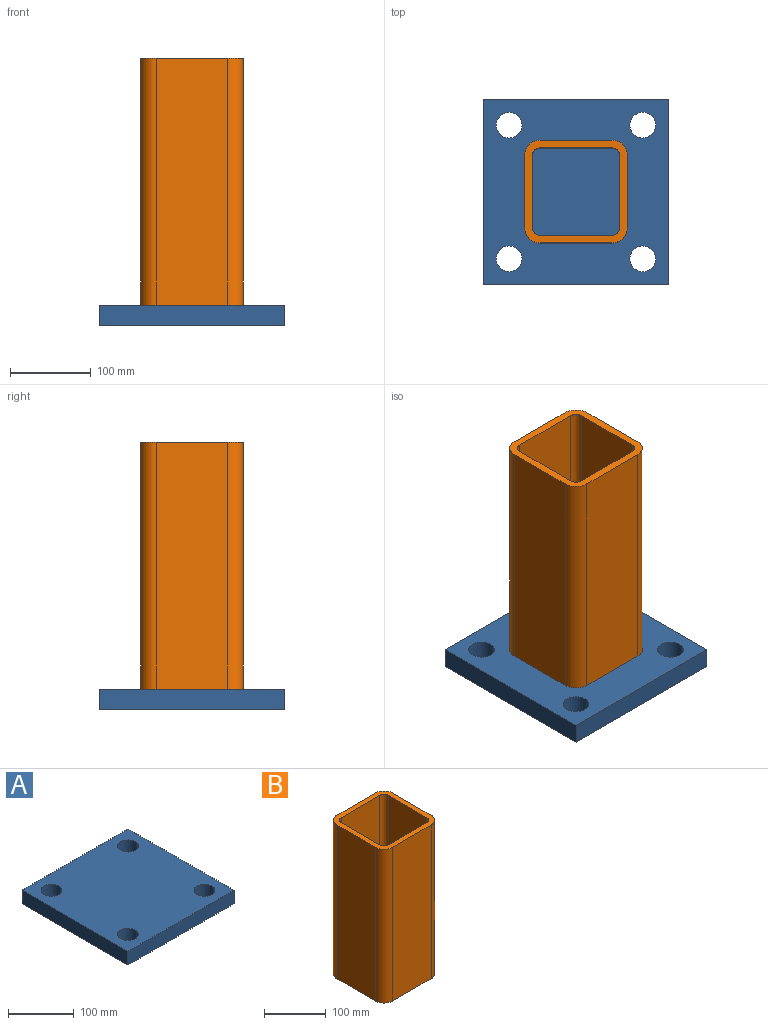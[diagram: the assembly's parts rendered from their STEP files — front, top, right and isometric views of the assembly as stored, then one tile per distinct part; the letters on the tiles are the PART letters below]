
ASSEMBLY  parts=2 mates=1
PART A: 10 faces, bbox 228.6x228.6x25.4 mm
  f0: plane 228.6x25.4mm, normal (-1,0,0), area 5806.4mm2, adj f1,f6,f8,f9
  f1: plane 228.6x25.4mm, normal (0,-1,0), area 5806.4mm2, adj f0,f2,f8,f9
  f2: plane 228.6x25.4mm, normal (1,0,0), area 5806.4mm2, adj f1,f6,f8,f9
  f3: cylinder r=15.88mm len=31.75mm, axis (0,0,-1), area 2533.5mm2, adj f8,f9
  f4: cylinder r=15.88mm len=31.75mm, axis (0,0,-1), area 2533.5mm2, adj f8,f9
  f5: cylinder r=15.88mm len=31.75mm, axis (0,0,-1), area 2533.5mm2, adj f8,f9
  f6: plane 228.6x25.4mm, normal (0,1,0), area 5806.4mm2, adj f0,f2,f8,f9
  f7: cylinder r=15.88mm len=31.75mm, axis (0,0,-1), area 2533.5mm2, adj f8,f9
  f8: plane 228.6x228.6mm, normal (0,0,1), area 49091mm2, adj f0,f1,f2,f3,f4,f5,f6,f7
  f9: plane 228.6x228.6mm, normal (0,0,-1), area 49091mm2, adj f0,f1,f2,f3,f4,f5,f6,f7
PART B: 18 faces, bbox 127x127x304.8 mm
  f0: plane 304.8x88.9mm, normal (0,-1,0), area 27096.7mm2, adj f1,f15,f16,f17
  f1: cylinder r=19.05mm len=304.8mm, axis (0,0,-1), area 9120.7mm2, adj f0,f2,f16,f17
  f2: plane 304.8x88.9mm, normal (1,0,0), area 27096.7mm2, adj f1,f3,f16,f17
  f3: cylinder r=19.05mm len=304.8mm, axis (0,0,-1), area 9120.7mm2, adj f2,f4,f16,f17
  f4: plane 304.8x88.9mm, normal (0,1,0), area 27096.7mm2, adj f3,f5,f16,f17
  f5: cylinder r=19.05mm len=304.8mm, axis (0,0,-1), area 9120.7mm2, adj f4,f6,f16,f17
  f6: plane 304.8x88.9mm, normal (-1,0,0), area 27096.7mm2, adj f5,f15,f16,f17
  f7: cylinder r=9.53mm len=304.8mm, axis (0,0,-1), area 4560.4mm2, adj f8,f14,f16,f17
  f8: plane 304.8x88.9mm, normal (1,0,0), area 27096.7mm2, adj f7,f9,f16,f17
  f9: cylinder r=9.53mm len=304.8mm, axis (0,0,-1), area 4560.4mm2, adj f8,f10,f16,f17
  f10: plane 304.8x88.9mm, normal (0,-1,0), area 27096.7mm2, adj f9,f11,f16,f17
  f11: cylinder r=9.53mm len=304.8mm, axis (0,0,-1), area 4560.4mm2, adj f10,f12,f16,f17
  f12: plane 304.8x88.9mm, normal (-1,0,0), area 27096.7mm2, adj f11,f13,f16,f17
  f13: cylinder r=9.53mm len=304.8mm, axis (0,0,-1), area 4560.4mm2, adj f12,f14,f16,f17
  f14: plane 304.8x88.9mm, normal (0,1,0), area 27096.7mm2, adj f7,f13,f16,f17
  f15: cylinder r=19.05mm len=304.8mm, axis (0,0,-1), area 9120.7mm2, adj f0,f6,f16,f17
  f16: plane 127x127mm, normal (0,0,1), area 4242.2mm2, adj f0,f1,f2,f3,f4,f5,f6,f7
  f17: plane 127x127mm, normal (0,0,-1), area 4242.2mm2, adj f0,f1,f2,f3,f4,f5,f6,f7
PLACE A at identity fixed
PLACE B t=(0,0,25.4)mm
MATE fastened B.f17 <-> A.f8  axis (0,0,-1) through (0,0,25.4)mm
